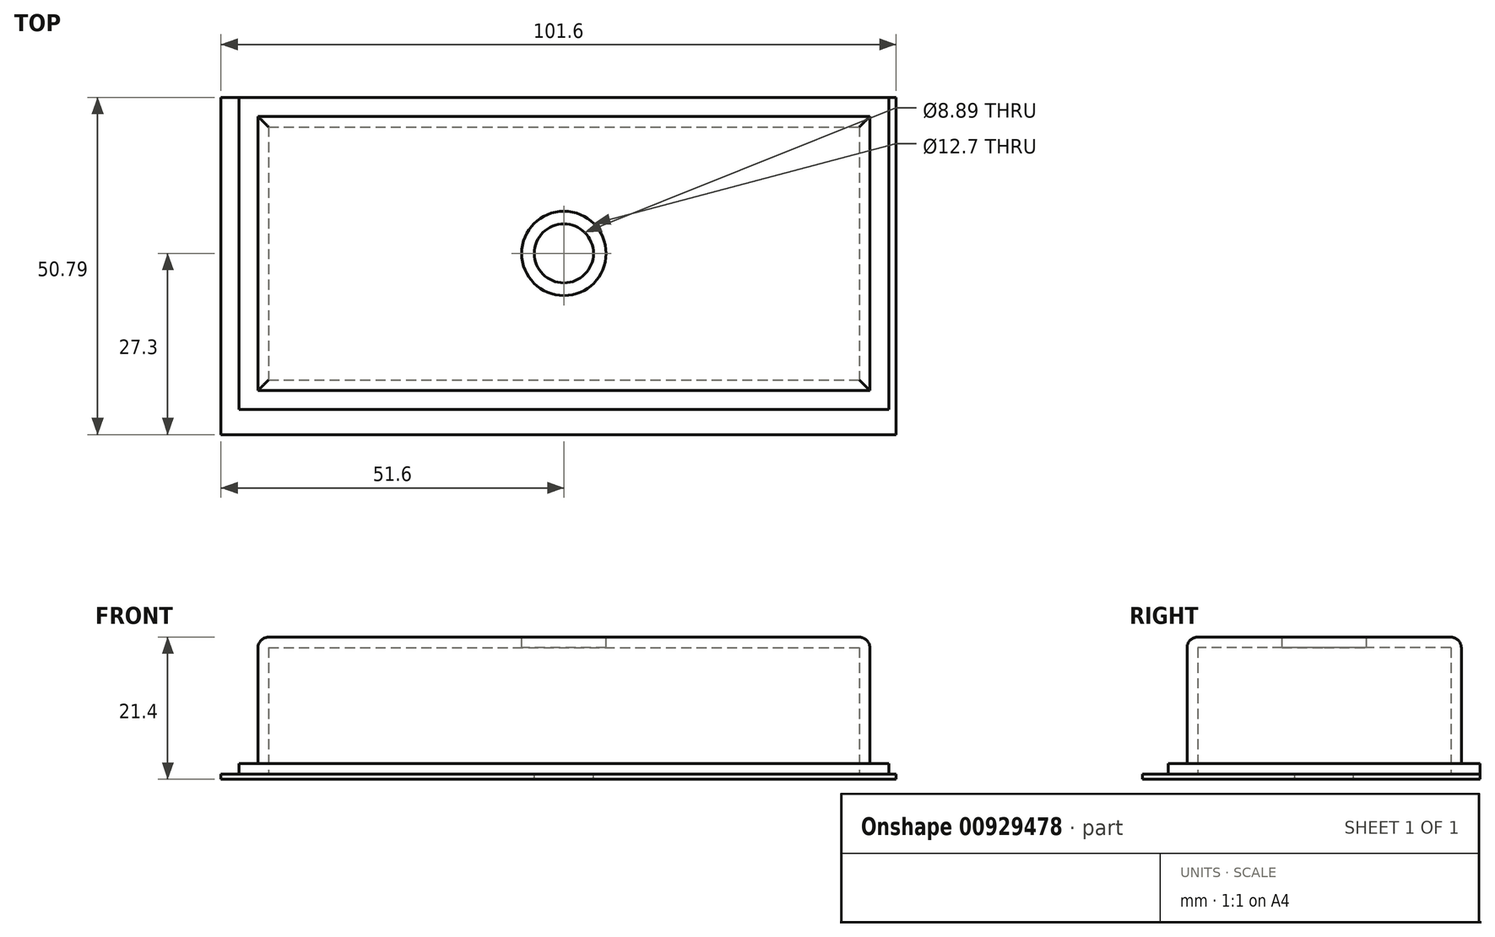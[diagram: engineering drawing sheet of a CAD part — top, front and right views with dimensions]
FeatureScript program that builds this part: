
annotation { "Feature Type Name" : "Feature", "Feature Type Description" : "" }
export const myFeature = defineFeature(function(context is Context, id is Id, definition is map)
    precondition{}
    {
        {
            var Q0;
            Q0=qCreatedBy(makeId("Top.planeOp"),FACE);
            var sketch = newSketch(context, id + "F0", { "sketchPlane" : qUnion([Q0])});
            skLineSegment(sketch, "E0.bottom", {"start": v(-44.45, 19.05) * mm, "end": v(44.45, 19.05) * mm});
            skLineSegment(sketch, "E0.top", {"start": v(-44.45, -19.05) * mm, "end": v(44.45, -19.05) * mm});
            skLineSegment(sketch, "E0.left", {"start": v(-44.45, 19.05) * mm, "end": v(-44.45, -19.05) * mm});
            skLineSegment(sketch, "E0.right", {"start": v(44.45, 19.05) * mm, "end": v(44.45, -19.05) * mm});
            skPoint(sketch, "E0.middle", {"position": v(0, 0) * mm});
            skSolve(sketch);
        }
        {
            var Q0;
            Q0=makeQuery(id+"F0.imprint","IMPRINT",FACE,{"disambiguationData":[TD([[makeQuery(id+"F0.imprint","IMPRINT",EDGE,{"derivedFrom":sQuery(id+"F0.wireOp",EDGE,"E0.bottom")}),-1.0]])]});
            extrude(context, id + "F1", {"entities" : qUnion([Q0]), "depth" : 17.46 * mm, "offsetDistance" : 25.4 * mm});
        }
        {
            var Q0;
            Q0=makeQuery(id+"F1.opExtrude","CAP_FACE",FACE,{"disambiguationData":[OSD([sQuery(id+"F0.wireOp",EDGE,"E0.bottom"),sQuery(id+"F0.wireOp",EDGE,"E0.top"),sQuery(id+"F0.wireOp",EDGE,"E0.left"),sQuery(id+"F0.wireOp",EDGE,"E0.right")])],"isStart":true});
            shell(context, id + "F2", {"entities" : qUnion([Q0]), "thickness" : 1.59 * mm, "oppositeDirection" : true});
        }
        {
            var Q0;
            Q0=makeQuery(id+"F1.opExtrude","CAP_FACE",FACE,{"disambiguationData":[OSD([sQuery(id+"F0.wireOp",EDGE,"E0.bottom"),sQuery(id+"F0.wireOp",EDGE,"E0.top"),sQuery(id+"F0.wireOp",EDGE,"E0.left"),sQuery(id+"F0.wireOp",EDGE,"E0.right")])],"isStart":true});
            var sketch = newSketch(context, id + "F3", { "sketchPlane" : qUnion([Q0])});
            skLineSegment(sketch, "E1.bottom", {"start": v(44.45, 19.05) * mm, "end": v(-44.45, 19.05) * mm});
            skLineSegment(sketch, "E1.top", {"start": v(44.45, -19.05) * mm, "end": v(-44.45, -19.05) * mm});
            skLineSegment(sketch, "E1.left", {"start": v(44.45, 19.05) * mm, "end": v(44.45, -19.05) * mm});
            skLineSegment(sketch, "E1.right", {"start": v(-44.45, 19.05) * mm, "end": v(-44.45, -19.05) * mm});
            skPoint(sketch, "E1.middle", {"position": v(0, 0) * mm});
            skLineSegment(sketch, "E2.bottom", {"start": v(48.9, 23.5) * mm, "end": v(-48.9, 23.5) * mm});
            skLineSegment(sketch, "E2.top", {"start": v(48.9, -23.5) * mm, "end": v(-48.9, -23.5) * mm});
            skLineSegment(sketch, "E2.left", {"start": v(48.9, 23.5) * mm, "end": v(48.9, -23.5) * mm});
            skLineSegment(sketch, "E2.right", {"start": v(-48.9, 23.5) * mm, "end": v(-48.9, -23.5) * mm});
            skSolve(sketch);
        }
        {
            var Q0;
            Q0=makeQuery(id+"F3.imprint","IMPRINT",FACE,{"disambiguationData":[TD([[makeQuery(id+"F3.imprint","IMPRINT",EDGE,{"derivedFrom":sQuery(id+"F3.wireOp",EDGE,"E1.bottom")}),1.0]])]});
            var Q1;
            Q1=makeQuery(id+"F3.imprint","IMPRINT",FACE,{"disambiguationData":[TD([[makeQuery(id+"F3.imprint","IMPRINT",EDGE,{"derivedFrom":sQuery(id+"F3.wireOp",EDGE,"E2.bottom")}),1.0]])]});
            extrude(context, id + "F4", {"entities" : qUnion([Q0, Q1]), "operationType" : NewBodyOperationType.ADD, "depth" : 1.59 * mm, "offsetDistance" : 25.4 * mm});
        }
        {
            var Q0;
            Q0=makeQuery(id+"F1.opExtrude","CAP_FACE",FACE,{"disambiguationData":[OSD([sQuery(id+"F0.wireOp",EDGE,"E0.bottom"),sQuery(id+"F0.wireOp",EDGE,"E0.top"),sQuery(id+"F0.wireOp",EDGE,"E0.left"),sQuery(id+"F0.wireOp",EDGE,"E0.right")])],"isStart":false});
            fillet(context, id + "F5", {"entities" : qUnion([Q0]), "radius" : 1.59 * mm, "tangentPropagation" : true, "allowEdgeOverflow" : false});
        }
        {
            var Q0;
            Q0=makeQuery(id+"F1.opExtrude","CAP_FACE",FACE,{"disambiguationData":[OSD([sQuery(id+"F0.wireOp",EDGE,"E0.bottom"),sQuery(id+"F0.wireOp",EDGE,"E0.top"),sQuery(id+"F0.wireOp",EDGE,"E0.left"),sQuery(id+"F0.wireOp",EDGE,"E0.right")])],"isStart":false});
            var sketch = newSketch(context, id + "F6", { "sketchPlane" : qUnion([Q0])});
            skCircle(sketch, "E3", {"center": v(0, 0) * mm, "radius": 6.35 * mm});
            skSolve(sketch);
        }
        {
            var Q0;
            Q0 = qSketchRegion(id + "F6", true);
            extrude(context, id + "F7", {"entities" : qUnion([Q0]), "operationType" : NewBodyOperationType.REMOVE, "oppositeDirection" : true, "depth" : 25.4 * mm, "offsetDistance" : 25.4 * mm});
        }
        {
            var Q0;
            Q0=makeQuery(id+"F4.opExtrude","CAP_FACE",FACE,{"disambiguationData":[OSD([sQuery(id+"F3.wireOp",EDGE,"E1.bottom"),sQuery(id+"F3.wireOp",EDGE,"E1.top"),sQuery(id+"F3.wireOp",EDGE,"E1.left"),sQuery(id+"F3.wireOp",EDGE,"E1.right"),sQuery(id+"F3.wireOp",EDGE,"E2.bottom"),sQuery(id+"F3.wireOp",EDGE,"E2.top"),sQuery(id+"F3.wireOp",EDGE,"E2.left"),sQuery(id+"F3.wireOp",EDGE,"E2.right")])],"isStart":false});
            var sketch = newSketch(context, id + "F8", { "sketchPlane" : qUnion([Q0])});
            skLineSegment(sketch, "E4.bottom", {"start": v(-51.6, 27.3) * mm, "end": v(50, 27.3) * mm});
            skLineSegment(sketch, "E4.top", {"start": v(-51.6, -23.5) * mm, "end": v(50, -23.5) * mm});
            skLineSegment(sketch, "E4.left", {"start": v(-51.6, 27.3) * mm, "end": v(-51.6, -23.5) * mm});
            skLineSegment(sketch, "E4.right", {"start": v(50, 27.3) * mm, "end": v(50, -23.5) * mm});
            skSolve(sketch);
        }
        {
            var Q0;
            Q0=makeQuery(id+"F8.imprint","IMPRINT",FACE,{"disambiguationData":[TD([[makeQuery(id+"F8.imprint","IMPRINT",EDGE,{"derivedFrom":sQuery(id+"F8.wireOp",EDGE,"E4.bottom")}),-1.0]])]});
            var Q1;
            Q1=makeQuery(id+"F8.imprint","IMPRINT",FACE,{"disambiguationData":[TD([[makeQuery(id+"F8.imprint","IMPRINT",EDGE,{"derivedFrom":makeQuery(id+"F4.opExtrude","CAP_EDGE",EDGE,{"disambiguationData":[OSD([sQuery(id+"F3.wireOp",EDGE,"E1.bottom")])],"isStart":false})}),-1.0]])]});
            var Q2;
            Q2=makeQuery(id+"F8.imprint","IMPRINT",FACE,{"disambiguationData":[TD([[makeQuery(id+"F8.imprint","IMPRINT",EDGE,{"derivedFrom":makeQuery(id+"F4.opExtrude","CAP_EDGE",EDGE,{"disambiguationData":[OSD([sQuery(id+"F3.wireOp",EDGE,"E1.bottom")])],"isStart":false})}),1.0]])]});
            extrude(context, id + "F9", {"entities" : qUnion([Q0, Q1, Q2]), "depth" : 0.76 * mm, "offsetDistance" : 25.4 * mm});
        }
        {
            var Q0;
            Q0=makeQuery(id+"F9.opExtrude","CAP_FACE",FACE,{"disambiguationData":[OSD([sQuery(id+"F8.wireOp",EDGE,"E4.bottom"),sQuery(id+"F8.wireOp",EDGE,"E4.top"),sQuery(id+"F8.wireOp",EDGE,"E4.left"),sQuery(id+"F8.wireOp",EDGE,"E4.right")])],"isStart":true});
            var sketch = newSketch(context, id + "F10", { "sketchPlane" : qUnion([Q0])});
            skCircle(sketch, "E5", {"center": v(0, 0) * mm, "radius": 4.45 * mm});
            skSolve(sketch);
        }
        {
            var Q0;
            Q0=makeQuery(id+"F10.imprint","IMPRINT",FACE,{"disambiguationData":[TD([[makeQuery(id+"F10.imprint","IMPRINT",EDGE,{"derivedFrom":sQuery(id+"F10.wireOp",EDGE,"E5")}),1.0]])]});
            extrude(context, id + "F11", {"entities" : qUnion([Q0]), "operationType" : NewBodyOperationType.REMOVE, "endBound" : BoundingType.UP_TO_NEXT, "oppositeDirection" : true, "depth" : 25.4 * mm, "offsetDistance" : 25.4 * mm});
        }
    });
